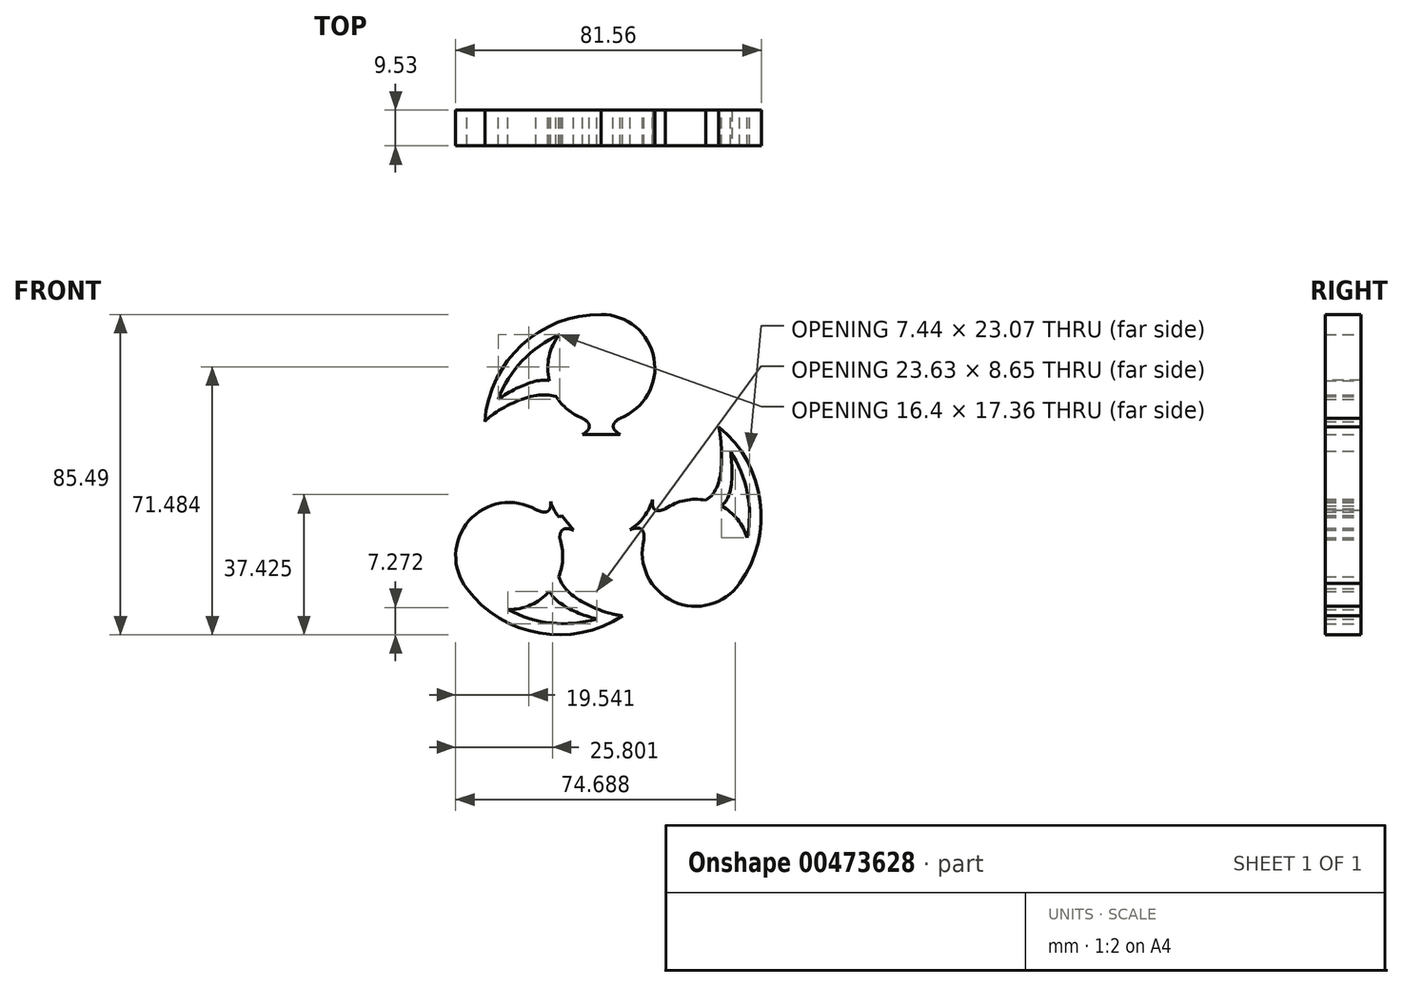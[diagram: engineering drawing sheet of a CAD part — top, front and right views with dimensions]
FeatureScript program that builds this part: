
annotation { "Feature Type Name" : "Feature", "Feature Type Description" : "" }
export const myFeature = defineFeature(function(context is Context, id is Id, definition is map)
    precondition{}
    {
        {
            var Q0;
            Q0=qCreatedBy(makeId("Front.planeOp"),FACE);
            var sketch = newSketch(context, id + "F0", { "sketchPlane" : qUnion([Q0])});
            skCircle(sketch, "E0", {"center": v(0, 0) * mm, "radius": 14.29 * mm});
            skLineSegment(sketch, "E1", {"start": v(0, 0) * mm, "end": v(0, 14.29) * mm});
            skLineSegment(sketch, "E2", {"start": v(0, 0) * mm, "end": v(-11.3, -8.76) * mm});
            skLineSegment(sketch, "E3", {"start": v(0, 0) * mm, "end": v(11.43, -8.57) * mm});
            skCircle(sketch, "E4", {"center": v(0, 31.12) * mm, "radius": 14.29 * mm});
            skLineSegment(sketch, "E5", {"start": v(0, 14.29) * mm, "end": v(0, 16.83) * mm});
            skArc(sketch, "E6", {"start": v(0, 45.4) * mm, "mid": v(-21.2, 37.27) * mm, "end": v(-31.1, 16.83) * mm});
            skFitSpline(sketch, "E7", {"points": [v(-31.1, 16.83) * mm, v(-17.35, 23.79) * mm, v(0, 16.83) * mm], "startDerivative": vector(18.3, 19.68) * mm, "endDerivative": vector(52.34, -33.11) * mm});
            skLineSegment(sketch, "E8", {"start": v(0, 15.56) * mm, "end": v(-3.18, 15.56) * mm});
            skPoint(sketch, "E8.endSnap0", {"position": v(0, 15.56) * mm});
            skLineSegment(sketch, "E9", {"start": v(0, 15.56) * mm, "end": v(3.18, 15.56) * mm});
            skLineSegment(sketch, "E10", {"start": v(0, 17.74) * mm, "end": v(5.03, 17.74) * mm});
            skLineSegment(sketch, "E11", {"start": v(0, 17.74) * mm, "end": v(-5.03, 17.74) * mm});
            skLineSegment(sketch, "E12", {"start": v(0, 14.29) * mm, "end": v(0, 13.37) * mm});
            skLineSegment(sketch, "E13", {"start": v(0, 13.37) * mm, "end": v(-5.03, 13.37) * mm});
            skLineSegment(sketch, "E14", {"start": v(0, 13.37) * mm, "end": v(5.03, 13.37) * mm});
            skFitSpline(sketch, "E15", {"points": [v(-5.03, 17.74) * mm, v(-3.18, 15.56) * mm, v(-5.03, 13.37) * mm], "startDerivative": vector(7.47, -4.37) * mm, "endDerivative": vector(-7.47, -4.37) * mm});
            skFitSpline(sketch, "E16", {"points": [v(5.03, 13.37) * mm, v(3.18, 15.56) * mm, v(5.03, 17.74) * mm], "startDerivative": vector(-7.47, 4.37) * mm, "endDerivative": vector(7.47, 4.37) * mm});
            skArc(sketch, "E17", {"start": v(4.36, 42.56) * mm, "mid": v(-16.61, 36.94) * mm, "end": v(-28.69, 18.9) * mm});
            skFitSpline(sketch, "E18", {"points": [v(-30.7, 19.98) * mm, v(-16.8, 27.72) * mm, v(0.44, 19.97) * mm], "startDerivative": vector(18.3, 19.68) * mm, "endDerivative": vector(52.34, -33.11) * mm});
            skLineSegment(sketch, "E19", {"start": v(-3.18, 15.56) * mm, "end": v(0, 14.29) * mm});
            skLineSegment(sketch, "E20", {"start": v(0, 14.29) * mm, "end": v(3.18, 15.56) * mm});
            skCircle(sketch, "E21", {"center": v(25.21, -18.22) * mm, "radius": 14.29 * mm});
            skLineSegment(sketch, "E22", {"start": v(11.43, -8.57) * mm, "end": v(13.51, -10.03) * mm});
            skArc(sketch, "E23", {"start": v(36.92, -26.42) * mm, "mid": v(42.42, -4.39) * mm, "end": v(31.34, 15.44) * mm});
            skFitSpline(sketch, "E24", {"points": [v(31.34, 15.44) * mm, v(30.71, -0.93) * mm, v(13.51, -10.03) * mm], "startDerivative": vector(5.62, -26.28) * mm, "endDerivative": vector(-57.15, -23.88) * mm});
            skLineSegment(sketch, "E25", {"start": v(12.47, -9.3) * mm, "end": v(14.3, -6.7) * mm});
            skPoint(sketch, "E25.endSnap0", {"position": v(12.47, -9.3) * mm});
            skLineSegment(sketch, "E26", {"start": v(12.47, -9.3) * mm, "end": v(10.65, -11.9) * mm});
            skLineSegment(sketch, "E27", {"start": v(14.26, -10.55) * mm, "end": v(11.38, -14.67) * mm});
            skLineSegment(sketch, "E28", {"start": v(14.26, -10.55) * mm, "end": v(17.14, -6.43) * mm});
            skArc(sketch, "E29", {"start": v(32.04, -28.23) * mm, "mid": v(39.54, -7.93) * mm, "end": v(31.84, 12.3) * mm});
            skFitSpline(sketch, "E30", {"points": [v(33.7, 13.3) * mm, v(33.83, -3.4) * mm, v(15.84, -12.2) * mm], "startDerivative": vector(5.62, -26.28) * mm, "endDerivative": vector(-57.15, -23.88) * mm});
            skLineSegment(sketch, "E31", {"start": v(14.3, -6.7) * mm, "end": v(11.8, -8.05) * mm});
            skLineSegment(sketch, "E32", {"start": v(11.43, -8.57) * mm, "end": v(10.65, -11.9) * mm});
            skLineSegment(sketch, "E33.0", {"start": v(14.3, -6.7) * mm, "end": v(12.47, -9.3) * mm, "construction": true});
            skCircle(sketch, "E34", {"center": v(-24.58, -19.07) * mm, "radius": 14.29 * mm});
            skLineSegment(sketch, "E35", {"start": v(-11.3, -8.76) * mm, "end": v(-13.26, -10.36) * mm});
            skArc(sketch, "E36", {"start": v(-35.91, -27.78) * mm, "mid": v(-16.54, -39.63) * mm, "end": v(5.7, -35.02) * mm});
            skFitSpline(sketch, "E37", {"points": [v(5.7, -35.02) * mm, v(-8.63, -28.76) * mm, v(-13.26, -10.36) * mm], "startDerivative": vector(-26.76, 2.52) * mm, "endDerivative": vector(-5.64, 61.68) * mm});
            skLineSegment(sketch, "E38", {"start": v(-12.27, -9.56) * mm, "end": v(-10.26, -12.02) * mm});
            skPoint(sketch, "E38.endSnap0", {"position": v(-12.27, -9.56) * mm});
            skLineSegment(sketch, "E39", {"start": v(-12.27, -9.56) * mm, "end": v(-14.28, -7.1) * mm});
            skLineSegment(sketch, "E40", {"start": v(-13.97, -10.94) * mm, "end": v(-17.43, -6.7) * mm});
            skLineSegment(sketch, "E41", {"start": v(-13.97, -10.94) * mm, "end": v(-11.04, -14.51) * mm});
            skArc(sketch, "E42", {"start": v(-36.27, -22.58) * mm, "mid": v(-19.07, -35.8) * mm, "end": v(2.57, -34.43) * mm});
            skFitSpline(sketch, "E43", {"points": [v(2.95, -36.62) * mm, v(-12.05, -30.77) * mm, v(-16.16, -11.65) * mm], "startDerivative": vector(-26.76, 2.52) * mm, "endDerivative": vector(-5.64, 61.68) * mm});
            skLineSegment(sketch, "E44", {"start": v(-10.26, -12.02) * mm, "end": v(-10.8, -9.23) * mm});
            skLineSegment(sketch, "E45", {"start": v(-11.3, -8.76) * mm, "end": v(-14.28, -7.1) * mm});
            skLineSegment(sketch, "E46.0", {"start": v(-10.26, -12.02) * mm, "end": v(-12.27, -9.56) * mm, "construction": true});
            skLineSegment(sketch, "E47", {"start": v(-11.3, -8.76) * mm, "end": v(-10.57, -8.2) * mm});
            skLineSegment(sketch, "E48", {"start": v(11.43, -8.57) * mm, "end": v(10.7, -8.02) * mm});
            skLineSegment(sketch, "E49", {"start": v(10.7, -8.02) * mm, "end": v(13.72, -4) * mm});
            skLineSegment(sketch, "E50", {"start": v(10.7, -8.02) * mm, "end": v(7.68, -12.05) * mm});
            skLineSegment(sketch, "E51", {"start": v(-10.57, -8.2) * mm, "end": v(-13.54, -4.56) * mm});
            skLineSegment(sketch, "E52", {"start": v(-10.57, -8.2) * mm, "end": v(-7.49, -12.17) * mm});
            skFitSpline(sketch, "E53", {"points": [v(-13.54, -4.56) * mm, v(-14.28, -7.1) * mm, v(-17.43, -6.7) * mm], "startDerivative": vector(0.73, -8.28) * mm, "endDerivative": vector(-8.38, 3.81) * mm});
            skFitSpline(sketch, "E54", {"points": [v(-11.04, -14.51) * mm, v(-10.26, -12.02) * mm, v(-7.49, -12.17) * mm], "startDerivative": vector(-0.57, 7.9) * mm, "endDerivative": vector(7.64, -3.14) * mm});
            skFitSpline(sketch, "E55", {"points": [v(7.68, -12.05) * mm, v(10.65, -11.9) * mm, v(11.38, -14.67) * mm], "startDerivative": vector(8.1, 3.32) * mm, "endDerivative": vector(-0.74, -8.6) * mm});
            skFitSpline(sketch, "E56", {"points": [v(13.72, -4) * mm, v(14.3, -6.7) * mm, v(17.14, -6.43) * mm], "startDerivative": vector(-1.06, -8.48) * mm, "endDerivative": vector(7.9, 3.59) * mm});
            skSolve(sketch);
        }
        {
            var Q0;
            {var subQ0=sQuery(id+"F0.wireOp",EDGE,"E6");var subQ1=sQuery(id+"F0.wireOp",EDGE,"E4");var subQ2=makeQuery(id+"F0.imprint","INTERSECT",VERTEX,{"derivedFrom":[subQ1,subQ0]});Q0=makeQuery(id+"F0.imprint","IMPRINT",FACE,{"disambiguationData":[TD([[makeQuery(id+"F0.imprint","IMPRINT",EDGE,{"disambiguationData":[TD([[subQ2,-1.0]])],"derivedFrom":subQ1}),-1.0]])]});}
            var Q1;
            {var subQ0=sQuery(id+"F0.wireOp",EDGE,"E18");var subQ1=sQuery(id+"F0.wireOp",EDGE,"E4");var subQ2=makeQuery(id+"F0.imprint","INTERSECT",VERTEX,{"derivedFrom":[subQ1,subQ0]});Q1=makeQuery(id+"F0.imprint","IMPRINT",FACE,{"disambiguationData":[TD([[makeQuery(id+"F0.imprint","IMPRINT",EDGE,{"disambiguationData":[TD([[subQ2,-1.0]])],"derivedFrom":subQ1}),-1.0]])]});}
            var Q2;
            {var subQ0=sQuery(id+"F0.wireOp",EDGE,"E7");var subQ1=sQuery(id+"F0.wireOp",EDGE,"E6");var subQ2=makeQuery(id+"F0.imprint","INTERSECT",VERTEX,{"derivedFrom":[subQ1,subQ0]});Q2=makeQuery(id+"F0.imprint","IMPRINT",FACE,{"disambiguationData":[TD([[makeQuery(id+"F0.imprint","IMPRINT",EDGE,{"disambiguationData":[TD([[subQ2,1.0]])],"derivedFrom":subQ1}),1.0]])]});}
            var Q3;
            {var subQ7=sQuery(id+"F0.wireOp",EDGE,"E10");Q3=makeQuery(id+"F0.imprint","IMPRINT",FACE,{"disambiguationData":[TD([[makeQuery(id+"F0.imprint","IMPRINT",EDGE,{"derivedFrom":subQ7}),1.0]])]});}
            var Q4;
            Q4=makeQuery(id+"F0.imprint","IMPRINT",FACE,{"disambiguationData":[TD([[makeQuery(id+"F0.imprint","IMPRINT",EDGE,{"derivedFrom":sQuery(id+"F0.wireOp",EDGE,"E1")}),1.0]])]});
            var Q5;
            Q5=makeQuery(id+"F0.imprint","IMPRINT",FACE,{"disambiguationData":[TD([[makeQuery(id+"F0.imprint","IMPRINT",EDGE,{"derivedFrom":sQuery(id+"F0.wireOp",EDGE,"E2")}),1.0]])]});
            var Q6;
            Q6=makeQuery(id+"F0.imprint","IMPRINT",FACE,{"disambiguationData":[TD([[makeQuery(id+"F0.imprint","IMPRINT",EDGE,{"derivedFrom":sQuery(id+"F0.wireOp",EDGE,"E1")}),-1.0]])]});
            var Q7;
            {var subQ7=sQuery(id+"F0.wireOp",EDGE,"E40");Q7=makeQuery(id+"F0.imprint","IMPRINT",FACE,{"disambiguationData":[TD([[makeQuery(id+"F0.imprint","IMPRINT",EDGE,{"derivedFrom":subQ7}),1.0]])]});}
            var Q8;
            {var subQ0=sQuery(id+"F0.wireOp",EDGE,"E36");var subQ1=sQuery(id+"F0.wireOp",EDGE,"E34");var subQ2=makeQuery(id+"F0.imprint","INTERSECT",VERTEX,{"derivedFrom":[subQ1,subQ0]});Q8=makeQuery(id+"F0.imprint","IMPRINT",FACE,{"disambiguationData":[TD([[makeQuery(id+"F0.imprint","IMPRINT",EDGE,{"disambiguationData":[TD([[subQ2,-1.0]])],"derivedFrom":subQ1}),-1.0]])]});}
            var Q9;
            {var subQ0=sQuery(id+"F0.wireOp",EDGE,"E43");var subQ1=sQuery(id+"F0.wireOp",EDGE,"E34");var subQ2=makeQuery(id+"F0.imprint","INTERSECT",VERTEX,{"derivedFrom":[subQ1,subQ0]});Q9=makeQuery(id+"F0.imprint","IMPRINT",FACE,{"disambiguationData":[TD([[makeQuery(id+"F0.imprint","IMPRINT",EDGE,{"disambiguationData":[TD([[subQ2,-1.0]])],"derivedFrom":subQ1}),-1.0]])]});}
            var Q10;
            {var subQ0=sQuery(id+"F0.wireOp",EDGE,"E37");var subQ1=sQuery(id+"F0.wireOp",EDGE,"E36");var subQ2=makeQuery(id+"F0.imprint","INTERSECT",VERTEX,{"derivedFrom":[subQ1,subQ0]});Q10=makeQuery(id+"F0.imprint","IMPRINT",FACE,{"disambiguationData":[TD([[makeQuery(id+"F0.imprint","IMPRINT",EDGE,{"disambiguationData":[TD([[subQ2,1.0]])],"derivedFrom":subQ1}),1.0]])]});}
            var Q11;
            {var subQ1=sQuery(id+"F0.wireOp",EDGE,"E34");var subQ3=sQuery(id+"F0.wireOp",EDGE,"E37");var subQ4=makeQuery(id+"F0.imprint","INTERSECT",VERTEX,{"derivedFrom":[subQ1,subQ3]});Q11=makeQuery(id+"F0.imprint","IMPRINT",FACE,{"disambiguationData":[TD([[makeQuery(id+"F0.imprint","IMPRINT",EDGE,{"disambiguationData":[TD([[subQ4,-1.0]])],"derivedFrom":subQ3}),-1.0]])]});}
            var Q12;
            {var subQ5=sQuery(id+"F0.wireOp",EDGE,"E27");Q12=makeQuery(id+"F0.imprint","IMPRINT",FACE,{"disambiguationData":[TD([[makeQuery(id+"F0.imprint","IMPRINT",EDGE,{"derivedFrom":subQ5}),1.0]])]});}
            var Q13;
            {var subQ0=sQuery(id+"F0.wireOp",EDGE,"E23");var subQ1=sQuery(id+"F0.wireOp",EDGE,"E21");var subQ2=makeQuery(id+"F0.imprint","INTERSECT",VERTEX,{"derivedFrom":[subQ1,subQ0]});Q13=makeQuery(id+"F0.imprint","IMPRINT",FACE,{"disambiguationData":[TD([[makeQuery(id+"F0.imprint","IMPRINT",EDGE,{"disambiguationData":[TD([[subQ2,-1.0]])],"derivedFrom":subQ1}),-1.0]])]});}
            var Q14;
            {var subQ0=sQuery(id+"F0.wireOp",EDGE,"E30");var subQ1=sQuery(id+"F0.wireOp",EDGE,"E21");var subQ2=makeQuery(id+"F0.imprint","INTERSECT",VERTEX,{"derivedFrom":[subQ1,subQ0]});Q14=makeQuery(id+"F0.imprint","IMPRINT",FACE,{"disambiguationData":[TD([[makeQuery(id+"F0.imprint","IMPRINT",EDGE,{"disambiguationData":[TD([[subQ2,-1.0]])],"derivedFrom":subQ1}),-1.0]])]});}
            var Q15;
            {var subQ0=sQuery(id+"F0.wireOp",EDGE,"E24");var subQ1=sQuery(id+"F0.wireOp",EDGE,"E23");var subQ2=makeQuery(id+"F0.imprint","INTERSECT",VERTEX,{"derivedFrom":[subQ1,subQ0]});Q15=makeQuery(id+"F0.imprint","IMPRINT",FACE,{"disambiguationData":[TD([[makeQuery(id+"F0.imprint","IMPRINT",EDGE,{"disambiguationData":[TD([[subQ2,1.0]])],"derivedFrom":subQ1}),1.0]])]});}
            var Q16;
            {var subQ0=sQuery(id+"F0.wireOp",EDGE,"E28");var subQ1=sQuery(id+"F0.wireOp",EDGE,"E21");var subQ2=makeQuery(id+"F0.imprint","INTERSECT",VERTEX,{"derivedFrom":[subQ1,subQ0]});Q16=makeQuery(id+"F0.imprint","IMPRINT",FACE,{"disambiguationData":[TD([[makeQuery(id+"F0.imprint","IMPRINT",EDGE,{"disambiguationData":[TD([[subQ2,1.0]])],"derivedFrom":subQ1}),1.0]])]});}
            var Q17;
            {var subQ3=sQuery(id+"F0.wireOp",EDGE,"E40");Q17=makeQuery(id+"F0.imprint","IMPRINT",FACE,{"disambiguationData":[TD([[makeQuery(id+"F0.imprint","IMPRINT",EDGE,{"derivedFrom":subQ3}),-1.0]])]});}
            var Q18;
            {var subQ0=sQuery(id+"F0.wireOp",EDGE,"E37");var subQ3=sQuery(id+"F0.wireOp",EDGE,"E41");var subQ5=makeQuery(id+"F0.imprint","INTERSECT",VERTEX,{"derivedFrom":[subQ0,subQ3]});Q18=makeQuery(id+"F0.imprint","IMPRINT",FACE,{"disambiguationData":[TD([[makeQuery(id+"F0.imprint","IMPRINT",EDGE,{"disambiguationData":[TD([[subQ5,-1.0]])],"derivedFrom":subQ0}),-1.0]])]});}
            var Q19;
            {var subQ0=sQuery(id+"F0.wireOp",EDGE,"E47");Q19=makeQuery(id+"F0.imprint","IMPRINT",FACE,{"disambiguationData":[TD([[makeQuery(id+"F0.imprint","IMPRINT",EDGE,{"derivedFrom":subQ0}),-1.0]])]});}
            var Q20;
            {var subQ0=sQuery(id+"F0.wireOp",EDGE,"E47");Q20=makeQuery(id+"F0.imprint","IMPRINT",FACE,{"disambiguationData":[TD([[makeQuery(id+"F0.imprint","IMPRINT",EDGE,{"derivedFrom":subQ0}),1.0]])]});}
            var Q21;
            {var subQ0=sQuery(id+"F0.wireOp",EDGE,"E45");Q21=makeQuery(id+"F0.imprint","IMPRINT",FACE,{"disambiguationData":[TD([[makeQuery(id+"F0.imprint","IMPRINT",EDGE,{"derivedFrom":subQ0}),-1.0]])]});}
            var Q22;
            {var subQ1=sQuery(id+"F0.wireOp",EDGE,"E0");var subQ3=sQuery(id+"F0.wireOp",EDGE,"E44");var subQ4=makeQuery(id+"F0.imprint","INTERSECT",VERTEX,{"derivedFrom":[subQ1,subQ3]});Q22=makeQuery(id+"F0.imprint","IMPRINT",FACE,{"disambiguationData":[TD([[makeQuery(id+"F0.imprint","IMPRINT",EDGE,{"disambiguationData":[TD([[subQ4,-1.0]])],"derivedFrom":subQ1}),-1.0]])]});}
            var Q23;
            {var subQ5=sQuery(id+"F0.wireOp",EDGE,"E38");Q23=makeQuery(id+"F0.imprint","IMPRINT",FACE,{"disambiguationData":[TD([[makeQuery(id+"F0.imprint","IMPRINT",EDGE,{"derivedFrom":subQ5}),-1.0]])]});}
            var Q24;
            {var subQ5=sQuery(id+"F0.wireOp",EDGE,"E39");Q24=makeQuery(id+"F0.imprint","IMPRINT",FACE,{"disambiguationData":[TD([[makeQuery(id+"F0.imprint","IMPRINT",EDGE,{"derivedFrom":subQ5}),1.0]])]});}
            var Q25;
            {var subQ2=sQuery(id+"F0.wireOp",EDGE,"E39");Q25=makeQuery(id+"F0.imprint","IMPRINT",FACE,{"disambiguationData":[TD([[makeQuery(id+"F0.imprint","IMPRINT",EDGE,{"derivedFrom":subQ2}),-1.0]])]});}
            var Q26;
            {var subQ5=sQuery(id+"F0.wireOp",EDGE,"E38");Q26=makeQuery(id+"F0.imprint","IMPRINT",FACE,{"disambiguationData":[TD([[makeQuery(id+"F0.imprint","IMPRINT",EDGE,{"derivedFrom":subQ5}),1.0]])]});}
            var Q27;
            {var subQ3=sQuery(id+"F0.wireOp",EDGE,"E27");Q27=makeQuery(id+"F0.imprint","IMPRINT",FACE,{"disambiguationData":[TD([[makeQuery(id+"F0.imprint","IMPRINT",EDGE,{"derivedFrom":subQ3}),-1.0]])]});}
            var Q28;
            {var subQ0=sQuery(id+"F0.wireOp",EDGE,"E24");var subQ3=sQuery(id+"F0.wireOp",EDGE,"E28");var subQ5=makeQuery(id+"F0.imprint","INTERSECT",VERTEX,{"derivedFrom":[subQ0,subQ3]});Q28=makeQuery(id+"F0.imprint","IMPRINT",FACE,{"disambiguationData":[TD([[makeQuery(id+"F0.imprint","IMPRINT",EDGE,{"disambiguationData":[TD([[subQ5,-1.0]])],"derivedFrom":subQ0}),-1.0]])]});}
            var Q29;
            {var subQ5=sQuery(id+"F0.wireOp",EDGE,"E25");Q29=makeQuery(id+"F0.imprint","IMPRINT",FACE,{"disambiguationData":[TD([[makeQuery(id+"F0.imprint","IMPRINT",EDGE,{"derivedFrom":subQ5}),-1.0]])]});}
            var Q30;
            {var subQ2=sQuery(id+"F0.wireOp",EDGE,"E25");Q30=makeQuery(id+"F0.imprint","IMPRINT",FACE,{"disambiguationData":[TD([[makeQuery(id+"F0.imprint","IMPRINT",EDGE,{"derivedFrom":subQ2}),1.0]])]});}
            var Q31;
            {var subQ0=sQuery(id+"F0.wireOp",EDGE,"E31");Q31=makeQuery(id+"F0.imprint","IMPRINT",FACE,{"disambiguationData":[TD([[makeQuery(id+"F0.imprint","IMPRINT",EDGE,{"derivedFrom":subQ0}),-1.0]])]});}
            var Q32;
            {var subQ0=sQuery(id+"F0.wireOp",EDGE,"E48");Q32=makeQuery(id+"F0.imprint","IMPRINT",FACE,{"disambiguationData":[TD([[makeQuery(id+"F0.imprint","IMPRINT",EDGE,{"derivedFrom":subQ0}),-1.0]])]});}
            var Q33;
            {var subQ0=sQuery(id+"F0.wireOp",EDGE,"E48");Q33=makeQuery(id+"F0.imprint","IMPRINT",FACE,{"disambiguationData":[TD([[makeQuery(id+"F0.imprint","IMPRINT",EDGE,{"derivedFrom":subQ0}),1.0]])]});}
            var Q34;
            {var subQ0=sQuery(id+"F0.wireOp",EDGE,"E32");Q34=makeQuery(id+"F0.imprint","IMPRINT",FACE,{"disambiguationData":[TD([[makeQuery(id+"F0.imprint","IMPRINT",EDGE,{"derivedFrom":subQ0}),-1.0]])]});}
            var Q35;
            {var subQ2=sQuery(id+"F0.wireOp",EDGE,"E26");Q35=makeQuery(id+"F0.imprint","IMPRINT",FACE,{"disambiguationData":[TD([[makeQuery(id+"F0.imprint","IMPRINT",EDGE,{"derivedFrom":subQ2}),-1.0]])]});}
            var Q36;
            {var subQ5=sQuery(id+"F0.wireOp",EDGE,"E26");Q36=makeQuery(id+"F0.imprint","IMPRINT",FACE,{"disambiguationData":[TD([[makeQuery(id+"F0.imprint","IMPRINT",EDGE,{"derivedFrom":subQ5}),1.0]])]});}
            var Q37;
            {var subQ1=sQuery(id+"F0.wireOp",EDGE,"E4");var subQ3=sQuery(id+"F0.wireOp",EDGE,"E7");var subQ4=makeQuery(id+"F0.imprint","INTERSECT",VERTEX,{"derivedFrom":[subQ1,subQ3]});Q37=makeQuery(id+"F0.imprint","IMPRINT",FACE,{"disambiguationData":[TD([[makeQuery(id+"F0.imprint","IMPRINT",EDGE,{"disambiguationData":[TD([[subQ4,-1.0]])],"derivedFrom":subQ3}),-1.0]])]});}
            var Q38;
            {var subQ0=sQuery(id+"F0.wireOp",EDGE,"E7");var subQ3=sQuery(id+"F0.wireOp",EDGE,"E11");var subQ5=makeQuery(id+"F0.imprint","INTERSECT",VERTEX,{"derivedFrom":[subQ0,subQ3]});Q38=makeQuery(id+"F0.imprint","IMPRINT",FACE,{"disambiguationData":[TD([[makeQuery(id+"F0.imprint","IMPRINT",EDGE,{"disambiguationData":[TD([[subQ5,-1.0]])],"derivedFrom":subQ0}),-1.0]])]});}
            var Q39;
            {var subQ5=sQuery(id+"F0.wireOp",EDGE,"E8");Q39=makeQuery(id+"F0.imprint","IMPRINT",FACE,{"disambiguationData":[TD([[makeQuery(id+"F0.imprint","IMPRINT",EDGE,{"derivedFrom":subQ5}),-1.0]])]});}
            var Q40;
            {var subQ0=sQuery(id+"F0.wireOp",EDGE,"E20");Q40=makeQuery(id+"F0.imprint","IMPRINT",FACE,{"disambiguationData":[TD([[makeQuery(id+"F0.imprint","IMPRINT",EDGE,{"derivedFrom":subQ0}),-1.0]])]});}
            var Q41;
            {var subQ0=sQuery(id+"F0.wireOp",EDGE,"E12");Q41=makeQuery(id+"F0.imprint","IMPRINT",FACE,{"disambiguationData":[TD([[makeQuery(id+"F0.imprint","IMPRINT",EDGE,{"derivedFrom":subQ0}),1.0]])]});}
            var Q42;
            {var subQ0=sQuery(id+"F0.wireOp",EDGE,"E12");Q42=makeQuery(id+"F0.imprint","IMPRINT",FACE,{"disambiguationData":[TD([[makeQuery(id+"F0.imprint","IMPRINT",EDGE,{"derivedFrom":subQ0}),-1.0]])]});}
            var Q43;
            {var subQ0=sQuery(id+"F0.wireOp",EDGE,"E19");Q43=makeQuery(id+"F0.imprint","IMPRINT",FACE,{"disambiguationData":[TD([[makeQuery(id+"F0.imprint","IMPRINT",EDGE,{"derivedFrom":subQ0}),-1.0]])]});}
            var Q44;
            {var subQ2=sQuery(id+"F0.wireOp",EDGE,"E8");Q44=makeQuery(id+"F0.imprint","IMPRINT",FACE,{"disambiguationData":[TD([[makeQuery(id+"F0.imprint","IMPRINT",EDGE,{"derivedFrom":subQ2}),1.0]])]});}
            var Q45;
            {var subQ2=sQuery(id+"F0.wireOp",EDGE,"E9");Q45=makeQuery(id+"F0.imprint","IMPRINT",FACE,{"disambiguationData":[TD([[makeQuery(id+"F0.imprint","IMPRINT",EDGE,{"derivedFrom":subQ2}),-1.0]])]});}
            var Q46;
            {var subQ5=sQuery(id+"F0.wireOp",EDGE,"E9");Q46=makeQuery(id+"F0.imprint","IMPRINT",FACE,{"disambiguationData":[TD([[makeQuery(id+"F0.imprint","IMPRINT",EDGE,{"derivedFrom":subQ5}),1.0]])]});}
            var Q47;
            {var subQ3=sQuery(id+"F0.wireOp",EDGE,"E10");Q47=makeQuery(id+"F0.imprint","IMPRINT",FACE,{"disambiguationData":[TD([[makeQuery(id+"F0.imprint","IMPRINT",EDGE,{"derivedFrom":subQ3}),-1.0]])]});}
            extrude(context, id + "F1", {"entities" : qUnion([Q0, Q1, Q2, Q3, Q4, Q5, Q6, Q7, Q8, Q9, Q10, Q11, Q12, Q13, Q14, Q15, Q16, Q17, Q18, Q19, Q20, Q21, Q22, Q23, Q24, Q25, Q26, Q27, Q28, Q29, Q30, Q31, Q32, Q33, Q34, Q35, Q36, Q37, Q38, Q39, Q40, Q41, Q42, Q43, Q44, Q45, Q46, Q47]), "depth" : 9.52 * mm});
        }
    });
